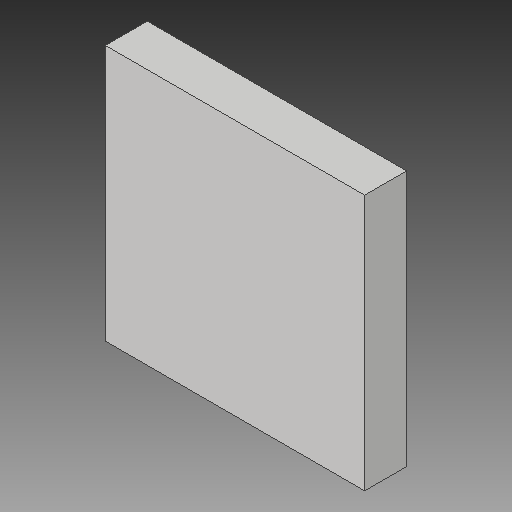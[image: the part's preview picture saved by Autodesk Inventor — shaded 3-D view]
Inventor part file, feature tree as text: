
AUTODESK INVENTOR PART (.ipt)
format: ipt  version: 2018 (Build 220112000, 112)  size: 82,944 bytes
history: native  units: in
note: dims shown in document units (in); Inventor stores cm internally (conversion verified against a paired STEP export)
features: other x1, extrude x1
ambient origin geometry x8: Origin, YZ Plane, XZ Plane, XY Plane, X Axis, Y Axis, Z Axis, Center Point
bodies: Solid1 (feature_tree)
feature tree (2):
  other  "PBTH, BSL_144"
  extrude  "Extrusion1"  Depth=0.0394in TaperAngle=0.0deg
